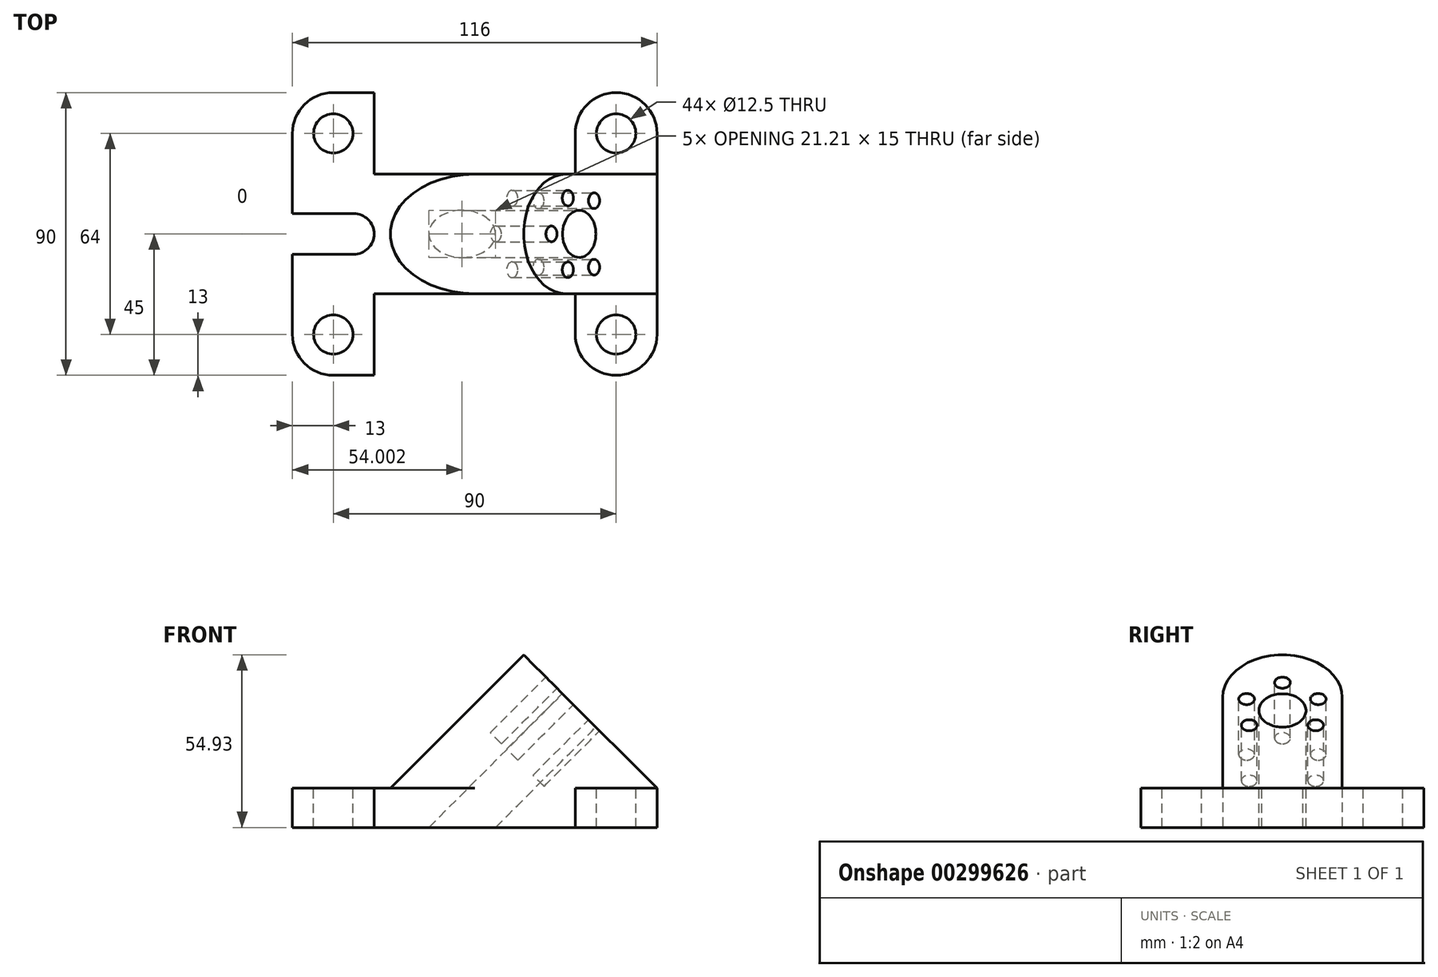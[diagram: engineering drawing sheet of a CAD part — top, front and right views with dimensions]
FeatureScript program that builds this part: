
annotation { "Feature Type Name" : "Feature", "Feature Type Description" : "" }
export const myFeature = defineFeature(function(context is Context, id is Id, definition is map)
    precondition{}
    {
        {
            var Q0;
            Q0=qCreatedBy(makeId("Front.planeOp"),FACE);
            var sketch = newSketch(context, id + "F0", { "sketchPlane" : qUnion([Q0])});
            skLineSegment(sketch, "E0", {"start": v(0, 0) * mm, "end": v(116, 0) * mm});
            skLineSegment(sketch, "E1", {"start": v(116, 0) * mm, "end": v(116, 12.5) * mm});
            skLineSegment(sketch, "E2", {"start": v(116, 12.5) * mm, "end": v(73.57, 54.93) * mm});
            skLineSegment(sketch, "E3", {"start": v(0, 0) * mm, "end": v(0, 12.5) * mm});
            skLineSegment(sketch, "E4", {"start": v(0, 12.5) * mm, "end": v(31.15, 12.5) * mm});
            skLineSegment(sketch, "E5", {"start": v(73.57, 54.93) * mm, "end": v(31.15, 12.5) * mm});
            skSolve(sketch);
        }
        {
            var Q0;
            Q0 = qSketchRegion(id + "F0", true);
            extrude(context, id + "F1", {"entities" : qUnion([Q0]), "depth" : 90 * mm});
        }
        {
            var Q0;
            Q0=makeQuery(id+"F1.opExtrude","SWEPT_FACE",FACE,{"disambiguationData":[OSD([sQuery(id+"F0.wireOp",EDGE,"E0")])]});
            var sketch = newSketch(context, id + "F2", { "sketchPlane" : qUnion([Q0])});
            skLineSegment(sketch, "E6", {"start": v(116, 90) * mm, "end": v(90, 90) * mm});
            skLineSegment(sketch, "E7", {"start": v(90, 90) * mm, "end": v(90, 64) * mm});
            skLineSegment(sketch, "E8", {"start": v(0, 90) * mm, "end": v(26, 90) * mm});
            skLineSegment(sketch, "E9", {"start": v(26, 90) * mm, "end": v(26, 64) * mm});
            skLineSegment(sketch, "E10", {"start": v(26, 64) * mm, "end": v(90, 64) * mm});
            skLineSegment(sketch, "E11", {"start": v(90, 90) * mm, "end": v(26, 90) * mm});
            skLineSegment(sketch, "E12", {"start": v(116, 0) * mm, "end": v(116, 26) * mm});
            skLineSegment(sketch, "E13", {"start": v(116, 26) * mm, "end": v(90, 26) * mm});
            skLineSegment(sketch, "E14", {"start": v(90, 26) * mm, "end": v(90, 0) * mm});
            skLineSegment(sketch, "E15", {"start": v(0, 0) * mm, "end": v(0, 26) * mm});
            skLineSegment(sketch, "E16", {"start": v(0, 26) * mm, "end": v(26, 26) * mm});
            skLineSegment(sketch, "E17", {"start": v(26, 26) * mm, "end": v(26, 0) * mm});
            skLineSegment(sketch, "E18", {"start": v(26, 0) * mm, "end": v(90, 0) * mm});
            skLineSegment(sketch, "E19", {"start": v(26, 26) * mm, "end": v(90, 26) * mm});
            skSolve(sketch);
        }
        {
            var Q0;
            Q0 = qSketchRegion(id + "F2", true);
            extrude(context, id + "F3", {"entities" : qUnion([Q0]), "operationType" : NewBodyOperationType.REMOVE, "oppositeDirection" : true, "depth" : 100 * mm});
        }
        {
            var Q0;
            Q0=makeQuery(id+"F3.boolean.opBoolean","COPY",FACE,{"derivedFrom":makeQuery(id+"F3.opExtrude","SWEPT_FACE",FACE,{"disambiguationData":[OSD([sQuery(id+"F2.wireOp",EDGE,"E14")])]})});
            var sketch = newSketch(context, id + "F4", { "sketchPlane" : qUnion([Q0])});
            skLineSegment(sketch, "E20", {"start": v(0, 38.5) * mm, "end": v(0, 12.5) * mm});
            skLineSegment(sketch, "E21", {"start": v(0, 12.5) * mm, "end": v(26, 12.5) * mm});
            skLineSegment(sketch, "E22", {"start": v(26, 12.5) * mm, "end": v(26, 38.5) * mm});
            skLineSegment(sketch, "E23", {"start": v(26, 38.5) * mm, "end": v(0, 38.5) * mm});
            skSolve(sketch);
        }
        {
            var Q0;
            Q0 = qSketchRegion(id + "F4", true);
            extrude(context, id + "F5", {"entities" : qUnion([Q0]), "operationType" : NewBodyOperationType.REMOVE, "oppositeDirection" : true, "depth" : 100 * mm});
        }
        {
            var Q0;
            Q0=makeQuery(id+"F3.boolean.opBoolean","COPY",FACE,{"derivedFrom":makeQuery(id+"F3.opExtrude","SWEPT_FACE",FACE,{"disambiguationData":[OSD([sQuery(id+"F2.wireOp",EDGE,"E7")])]})});
            var sketch = newSketch(context, id + "F6", { "sketchPlane" : qUnion([Q0])});
            skLineSegment(sketch, "E24", {"start": v(64, 38.5) * mm, "end": v(64, 12.5) * mm});
            skLineSegment(sketch, "E25", {"start": v(64, 12.5) * mm, "end": v(90, 12.5) * mm});
            skLineSegment(sketch, "E26", {"start": v(90, 12.5) * mm, "end": v(90, 38.5) * mm});
            skLineSegment(sketch, "E27", {"start": v(90, 38.5) * mm, "end": v(64, 38.5) * mm});
            skSolve(sketch);
        }
        {
            var Q0;
            Q0 = qSketchRegion(id + "F6", true);
            extrude(context, id + "F7", {"entities" : qUnion([Q0]), "operationType" : NewBodyOperationType.REMOVE, "oppositeDirection" : true, "depth" : 105 * mm});
        }
        {
            var Q0;
            Q0=makeQuery(id+"F1.opExtrude","CAP_EDGE",EDGE,{"disambiguationData":[OSD([sQuery(id+"F0.wireOp",EDGE,"E3")])],"isStart":true});
            var Q1;
            Q1=makeQuery(id+"F3.boolean.opBoolean","COPY",EDGE,{"derivedFrom":makeQuery(id+"F3.opExtrude","SWEPT_EDGE",EDGE,{"disambiguationData":[OSD([sQuery(id+"F0.wireOp",EDGE,"E0"),sQuery(id+"F2.wireOp",EDGE,"E17"),sQuery(id+"F2.wireOp",EDGE,"E18")])]})});
            var Q2;
            Q2=makeQuery(id+"F1.opExtrude","CAP_EDGE",EDGE,{"disambiguationData":[OSD([sQuery(id+"F0.wireOp",EDGE,"E1")])],"isStart":false});
            var Q3;
            Q3=makeQuery(id+"F3.boolean.opBoolean","COPY",EDGE,{"derivedFrom":makeQuery(id+"F3.opExtrude","SWEPT_EDGE",EDGE,{"disambiguationData":[OSD([sQuery(id+"F2.wireOp",EDGE,"E6"),sQuery(id+"F2.wireOp",EDGE,"E7"),sQuery(id+"F2.wireOp",EDGE,"E11")])]})});
            var Q4;
            Q4=makeQuery(id+"F3.boolean.opBoolean","COPY",EDGE,{"derivedFrom":makeQuery(id+"F3.opExtrude","SWEPT_EDGE",EDGE,{"disambiguationData":[OSD([sQuery(id+"F2.wireOp",EDGE,"E8"),sQuery(id+"F2.wireOp",EDGE,"E9"),sQuery(id+"F2.wireOp",EDGE,"E11")])]})});
            var Q5;
            Q5=makeQuery(id+"F1.opExtrude","CAP_EDGE",EDGE,{"disambiguationData":[OSD([sQuery(id+"F0.wireOp",EDGE,"E3")])],"isStart":false});
            var Q6;
            Q6=makeQuery(id+"F1.opExtrude","CAP_EDGE",EDGE,{"disambiguationData":[OSD([sQuery(id+"F0.wireOp",EDGE,"E1")])],"isStart":true});
            var Q7;
            Q7=makeQuery(id+"F3.boolean.opBoolean","COPY",EDGE,{"derivedFrom":makeQuery(id+"F3.opExtrude","SWEPT_EDGE",EDGE,{"disambiguationData":[OSD([sQuery(id+"F0.wireOp",EDGE,"E0"),sQuery(id+"F2.wireOp",EDGE,"E14"),sQuery(id+"F2.wireOp",EDGE,"E18")])]})});
            fillet(context, id + "F8", {"entities" : qUnion([Q0, Q1, Q2, Q3, Q4, Q5, Q6, Q7]), "radius" : 13 * mm, "tangentPropagation" : true, "allowEdgeOverflow" : false});
        }
        {
            var Q0;
            Q0=makeQuery(id+"F3.boolean.opBoolean","INTERSECT",EDGE,{"derivedFrom":[makeQuery(id+"F1.opExtrude","SWEPT_FACE",FACE,{"disambiguationData":[OSD([sQuery(id+"F0.wireOp",EDGE,"E5")])]}),makeQuery(id+"F3.opExtrude","SWEPT_FACE",FACE,{"disambiguationData":[OSD([sQuery(id+"F2.wireOp",EDGE,"E10")])]})]});
            var Q1;
            Q1=makeQuery(id+"F3.boolean.opBoolean","INTERSECT",EDGE,{"derivedFrom":[makeQuery(id+"F1.opExtrude","SWEPT_FACE",FACE,{"disambiguationData":[OSD([sQuery(id+"F0.wireOp",EDGE,"E5")])]}),makeQuery(id+"F3.opExtrude","SWEPT_FACE",FACE,{"disambiguationData":[OSD([sQuery(id+"F2.wireOp",EDGE,"E19")])]})]});
            fillet(context, id + "F9", {"entities" : qUnion([Q0, Q1]), "radius" : 19 * mm, "tangentPropagation" : true, "allowEdgeOverflow" : false});
        }
        {
            var Q0;
            Q0=makeQuery(id+"F1.opExtrude","SWEPT_FACE",FACE,{"disambiguationData":[OSD([sQuery(id+"F0.wireOp",EDGE,"E2")])]});
            var sketch = newSketch(context, id + "F10", { "sketchPlane" : qUnion([Q0])});
            skLineSegment(sketch, "E28", {"start": v(-26, -73.19) * mm, "end": v(-45, -73.19) * mm});
            skCircle(sketch, "E29", {"center": v(-45, -38.19) * mm, "radius": 7.5 * mm});
            skCircle(sketch, "E30", {"center": v(-45, -25.69) * mm, "radius": 2.5 * mm});
            skCircle(sketch, "E31", {"center": v(-33.6, -33.05) * mm, "radius": 2.5 * mm});
            skCircle(sketch, "E32", {"center": v(-56.4, -33.05) * mm, "radius": 2.5 * mm});
            skCircle(sketch, "E33", {"center": v(-55.57, -44.85) * mm, "radius": 2.5 * mm});
            skCircle(sketch, "E34", {"center": v(-34.43, -44.85) * mm, "radius": 2.5 * mm});
            skSolve(sketch);
        }
        {
            var Q0;
            Q0 = qSketchRegion(id + "F10", true);
            extrude(context, id + "F11", {"entities" : qUnion([Q0]), "operationType" : NewBodyOperationType.REMOVE, "oppositeDirection" : true, "depth" : 25 * mm});
        }
        {
            var Q0;
            Q0=makeQuery(id+"F1.opExtrude","SWEPT_FACE",FACE,{"disambiguationData":[OSD([sQuery(id+"F0.wireOp",EDGE,"E4")])]});
            var sketch = newSketch(context, id + "F12", { "sketchPlane" : qUnion([Q0])});
            skLineSegment(sketch, "E35", {"start": v(0, -13) * mm, "end": v(13, -13) * mm});
            skLineSegment(sketch, "E36", {"start": v(0, -77) * mm, "end": v(13, -77) * mm});
            skCircle(sketch, "E37", {"center": v(13, -13) * mm, "radius": 6.25 * mm});
            skCircle(sketch, "E38", {"center": v(13, -77) * mm, "radius": 6.25 * mm});
            skSolve(sketch);
        }
        {
            var Q0;
            Q0 = qSketchRegion(id + "F12", true);
            extrude(context, id + "F13", {"entities" : qUnion([Q0]), "operationType" : NewBodyOperationType.REMOVE, "oppositeDirection" : true, "depth" : 25 * mm});
        }
        {
            var Q0;
            Q0=makeQuery(id+"F5.boolean.opBoolean","COPY",FACE,{"derivedFrom":makeQuery(id+"F5.opExtrude","SWEPT_FACE",FACE,{"disambiguationData":[OSD([sQuery(id+"F4.wireOp",EDGE,"E21")])]})});
            var sketch = newSketch(context, id + "F14", { "sketchPlane" : qUnion([Q0])});
            skLineSegment(sketch, "E39", {"start": v(90, -13) * mm, "end": v(103, -13) * mm});
            skCircle(sketch, "E40", {"center": v(103, -13) * mm, "radius": 6.25 * mm});
            skSolve(sketch);
        }
        {
            var Q0;
            Q0 = qSketchRegion(id + "F14", true);
            extrude(context, id + "F15", {"entities" : qUnion([Q0]), "operationType" : NewBodyOperationType.REMOVE, "oppositeDirection" : true, "depth" : 25 * mm});
        }
        {
            var Q0;
            Q0=makeQuery(id+"F7.boolean.opBoolean","COPY",FACE,{"derivedFrom":makeQuery(id+"F7.opExtrude","SWEPT_FACE",FACE,{"disambiguationData":[OSD([sQuery(id+"F6.wireOp",EDGE,"E25")])]})});
            var sketch = newSketch(context, id + "F16", { "sketchPlane" : qUnion([Q0])});
            skLineSegment(sketch, "E41", {"start": v(90, -77) * mm, "end": v(103, -77) * mm});
            skCircle(sketch, "E42", {"center": v(103, -77) * mm, "radius": 6.25 * mm});
            skSolve(sketch);
        }
        {
            var Q0;
            Q0 = qSketchRegion(id + "F16", true);
            extrude(context, id + "F17", {"entities" : qUnion([Q0]), "operationType" : NewBodyOperationType.REMOVE, "oppositeDirection" : true, "depth" : 25 * mm});
        }
        {
            var Q0;
            Q0=makeQuery(id+"F1.opExtrude","SWEPT_FACE",FACE,{"disambiguationData":[OSD([sQuery(id+"F0.wireOp",EDGE,"E4")])]});
            var sketch = newSketch(context, id + "F18", { "sketchPlane" : qUnion([Q0])});
            skLineSegment(sketch, "E43", {"start": v(0, -13) * mm, "end": v(0, -45) * mm});
            skLineSegment(sketch, "E44", {"start": v(0, -45) * mm, "end": v(0, -38.5) * mm});
            skLineSegment(sketch, "E45", {"start": v(0, -38.5) * mm, "end": v(0, -45) * mm});
            skLineSegment(sketch, "E46", {"start": v(0, -45) * mm, "end": v(0, -51.5) * mm});
            skLineSegment(sketch, "E47", {"start": v(0, -51.5) * mm, "end": v(19.5, -51.5) * mm});
            skLineSegment(sketch, "E48", {"start": v(26, -45) * mm, "end": v(26, -45) * mm});
            skLineSegment(sketch, "E49", {"start": v(19.5, -38.5) * mm, "end": v(0, -38.5) * mm});
            skPoint(sketch, "E50.visualSharp", {"position": v(26, -38.5) * mm});
            skArc(sketch, "E50.filletArc", {"start": v(26, -45) * mm, "mid": v(24.1, -40.4) * mm, "end": v(19.5, -38.5) * mm});
            skPoint(sketch, "E51.visualSharp", {"position": v(26, -51.5) * mm});
            skArc(sketch, "E51.filletArc", {"start": v(19.5, -51.5) * mm, "mid": v(24.1, -49.6) * mm, "end": v(26, -45) * mm});
            skSolve(sketch);
        }
        {
            var Q0;
            Q0 = qSketchRegion(id + "F18", true);
            extrude(context, id + "F19", {"entities" : qUnion([Q0]), "operationType" : NewBodyOperationType.REMOVE, "oppositeDirection" : true, "depth" : 25 * mm});
        }
        {
            var Q0;
            Q0=makeQuery(id+"F1.opExtrude","SWEPT_FACE",FACE,{"disambiguationData":[OSD([sQuery(id+"F0.wireOp",EDGE,"E2")])]});
            var sketch = newSketch(context, id + "F20", { "sketchPlane" : qUnion([Q0])});
            skCircle(sketch, "E52", {"center": v(-45, -38.19) * mm, "radius": 7.5 * mm});
            skSolve(sketch);
        }
        {
            var Q0;
            Q0 = qSketchRegion(id + "F20", true);
            extrude(context, id + "F21", {"entities" : qUnion([Q0]), "operationType" : NewBodyOperationType.REMOVE, "oppositeDirection" : true, "depth" : 100 * mm});
        }
    });
